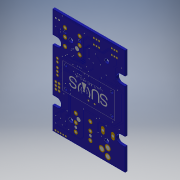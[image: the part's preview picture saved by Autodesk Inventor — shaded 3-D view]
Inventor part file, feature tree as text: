
AUTODESK INVENTOR PART (.ipt)
format: ipt  version: 2016 (Build 200138000, 138)  size: 371,200 bytes
history: native  units: mm
features: sketch x7, other x4, extrude x3, hole x2
ambient origin geometry x8: Origin, YZ Plane, XZ Plane, XY Plane, X Axis, Y Axis, Z Axis, Center Point
bodies: Solid1 (feature_tree)
feature tree (16):
  extrude  "Extrusion1"  Depth=82.66mm
  extrude  "Extrusion2"  Depth=28.305mm
  hole  "Hole1"  [1 undecoded]
  hole  "Hole2"  [1 undecoded]
  extrude  "Extrusion3"  Depth=1.7mm
  other  "Decal1"
  other  "Decal2"
  sketch  "Sketch1"  dims[d0=56.61mm d1=82.66mm]
  sketch  "Sketch2"  dims[d2=41.33mm d3=28.305mm]
  sketch  "Sketch3"  dims[d4=1.7mm d5=0.0mm d6=6.63mm]
  sketch  "Sketch4"  dims[d8=6.62mm d9=10.0mm]
  sketch  "Sketch5"  dims[d10=1.7mm d11=0.0mm d12=14.31mm]
  sketch  "Sketch6"  dims[d13=14.33mm]
  other  "Image1"
  sketch  "Sketch7"  dims[d14=28.0mm d15=28.0mm d16=54.0mm d17=14.33mm d18=14.31mm d19=54.0mm d20=3.2mm d21=6.0mm d22=4.0mm d23=2.0mm d24=90.0deg d25=8.0mm d26=20.594885mm d27=40.86mm d28=20.9mm d29=20.43mm d30=20.43mm d31=41.33mm d32=41.33mm d33=20.9mm d34=36.0mm d35=16.0mm d36=28.305mm d37=56.61mm d38=82.66mm d39=41.33mm d40=2.0mm d41=6.0mm d42=4.0mm d43=2.0mm d44=90.0deg d45=8.0mm d46=20.594885mm d47=9.77mm d48=11.26mm d49=21.2mm d50=11.26mm d51=2.0mm d52=2.0mm d53=11.43mm d54=10.0mm d55=0.0mm]
  other  "Image2"
note: 2 required parameter values undecoded (feature->parameter linkage not recoverable at this tier; creation-order binding heuristic only, values carry confidence <= 0.55)
